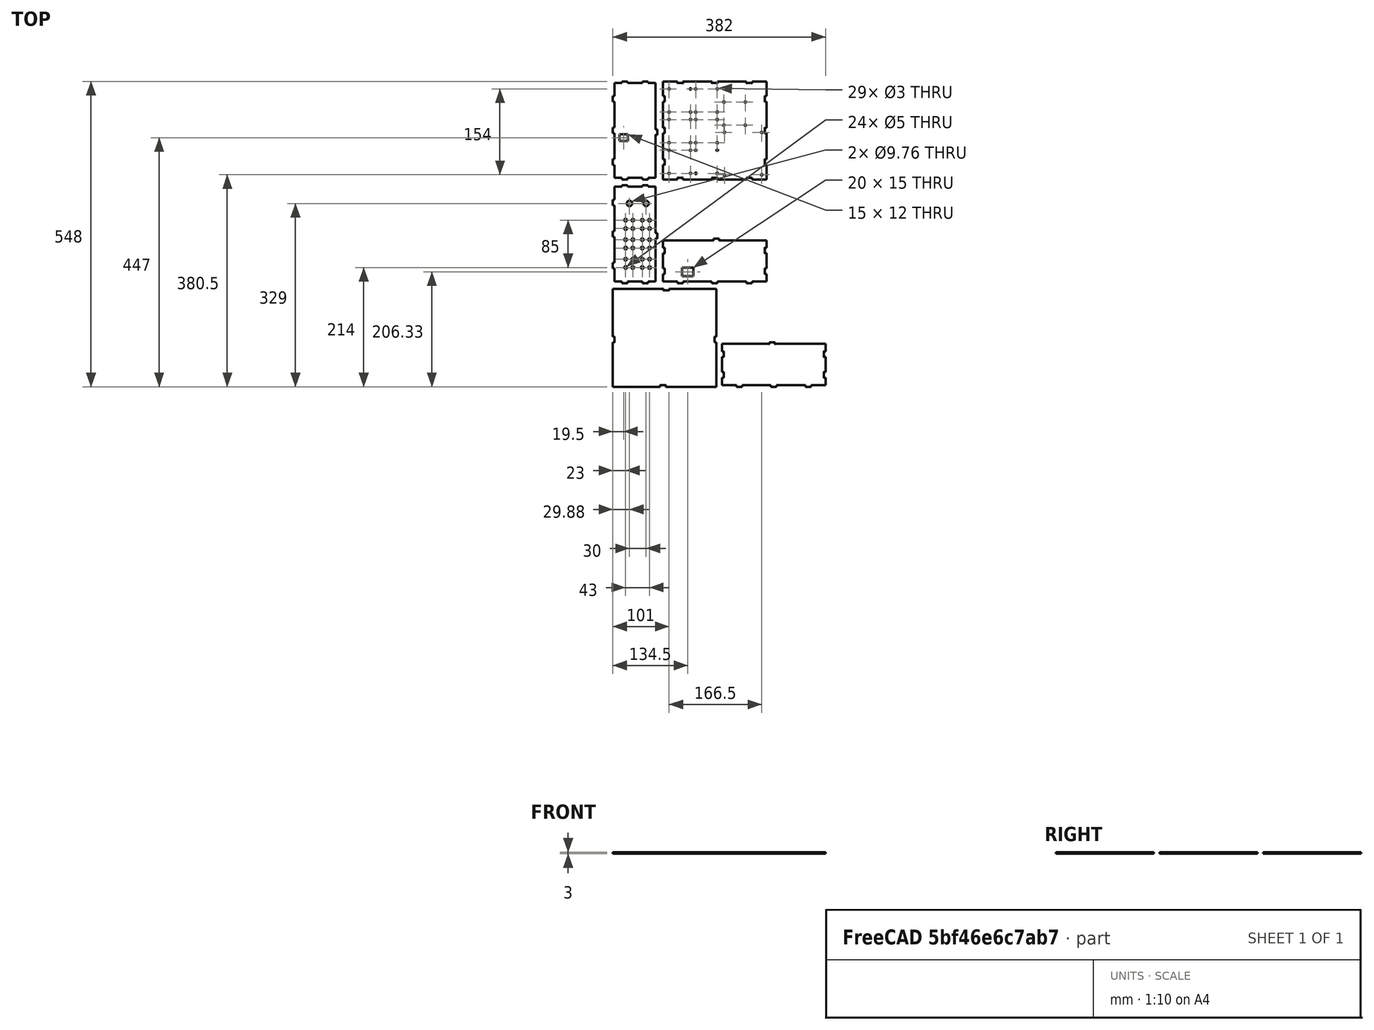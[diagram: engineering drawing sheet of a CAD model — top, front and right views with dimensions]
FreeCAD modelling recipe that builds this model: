
FCSTD DOCUMENT  (FreeCAD 0.20R29177 +426 (Git))
Label: exported_shapes
License: All rights reserved
LicenseURL: http://en.wikipedia.org/wiki/All_rights_reserved
objects: Part::Feature×6, Part::Part2DObjectPython×6
note: 12 computed .brp shape members not serialized (recipe doc carries the construction recipe); baked Part::Feature solids carry a one-line shape summary decoded from their .brp

FEATURE [Part::Feature] test
  Placement = pos=(93,88,70) rot=(0,-1,0;3.14159rad)
  shape: bbox 186 x 176 x 3 mm, 30 faces (baked)
FEATURE [Part::Feature] test001
  Placement = pos=(289,40,118) rot=(-1,0,0;1.5708rad)
  shape: bbox 186 x 80 x 3 mm, 48 faces (baked)
FEATURE [Part::Feature] test002
  Placement = pos=(40,274,123) rot=(0,1,0;1.5708rad)
  shape: bbox 80 x 176 x 3 mm, 66 faces (baked)
FEATURE [Part::Feature] test003
  Placement = pos=(183,226,-55) rot=(-1,0,0;1.5708rad)
  shape: bbox 186 x 80 x 3 mm, 52 faces (baked)
FEATURE [Part::Feature] test004
  Placement = pos=(40,460,-60) rot=(0,1,0;1.5708rad)
  shape: bbox 80 x 176 x 3 mm, 44 faces (baked)
FEATURE [Part::Feature] test005
  Placement = pos=(183,460,-7) rot=(0,-1,0;3.14159rad)
  shape: bbox 186 x 176 x 3 mm, 116 faces, 2 solids (baked)
FEATURE [Part::Part2DObjectPython] Shape2DView  # Draft 2D object (typed FeaturePython)
  AutoUpdate = true
  Base = -> test
  Clip = false
  FuseArch = false
  HiddenLines = false
  InPlace = true
  OnlySolids = false
  Projection = (0,0,1)
  ProjectionMode = 0
  SegmentLength = 0.05
  Tessellation = false
  VisibleOnly = false
FEATURE [Part::Part2DObjectPython] Shape2DView001  # Draft 2D object (typed FeaturePython)
  AutoUpdate = true
  Base = -> test001
  Clip = false
  FuseArch = false
  HiddenLines = false
  InPlace = true
  OnlySolids = false
  Projection = (0,0,1)
  ProjectionMode = 0
  SegmentLength = 0.05
  Tessellation = false
  VisibleOnly = false
FEATURE [Part::Part2DObjectPython] Shape2DView002  # Draft 2D object (typed FeaturePython)
  AutoUpdate = true
  Base = -> test002
  Clip = false
  FuseArch = false
  HiddenLines = false
  InPlace = true
  OnlySolids = false
  Projection = (0,0,1)
  ProjectionMode = 0
  SegmentLength = 0.05
  Tessellation = false
  VisibleOnly = false
FEATURE [Part::Part2DObjectPython] Shape2DView003  # Draft 2D object (typed FeaturePython)
  AutoUpdate = true
  Base = -> test003
  Clip = false
  FuseArch = false
  HiddenLines = false
  InPlace = true
  OnlySolids = false
  Projection = (0,0,1)
  ProjectionMode = 0
  SegmentLength = 0.05
  Tessellation = false
  VisibleOnly = false
FEATURE [Part::Part2DObjectPython] Shape2DView004  # Draft 2D object (typed FeaturePython)
  AutoUpdate = true
  Base = -> test004
  Clip = false
  FuseArch = false
  HiddenLines = false
  InPlace = true
  OnlySolids = false
  Projection = (0,0,1)
  ProjectionMode = 0
  SegmentLength = 0.05
  Tessellation = false
  VisibleOnly = false
FEATURE [Part::Part2DObjectPython] Shape2DView005  # Draft 2D object (typed FeaturePython)
  AutoUpdate = true
  Base = -> test005
  Clip = false
  FuseArch = false
  HiddenLines = false
  InPlace = true
  OnlySolids = false
  Projection = (0,0,1)
  ProjectionMode = 0
  SegmentLength = 0.05
  Tessellation = false
  VisibleOnly = false
